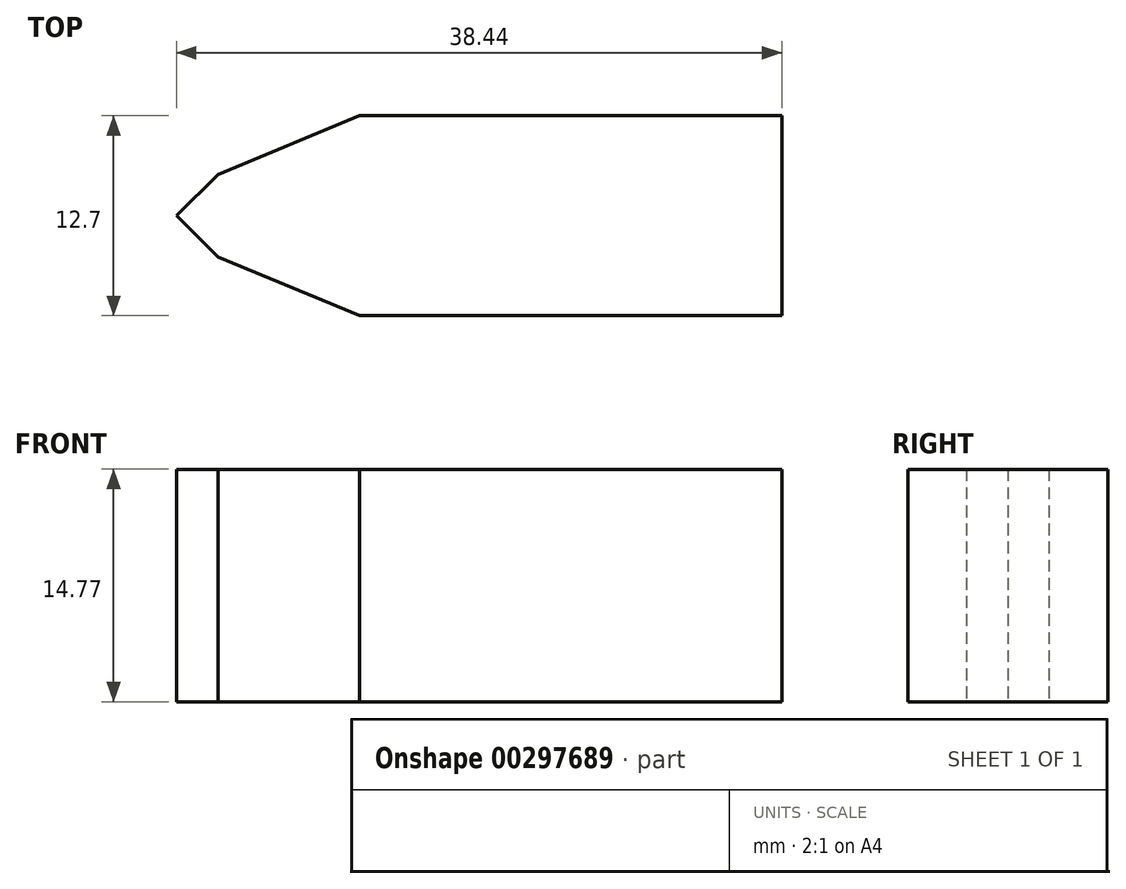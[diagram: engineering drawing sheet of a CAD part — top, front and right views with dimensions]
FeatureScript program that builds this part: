
annotation { "Feature Type Name" : "Feature", "Feature Type Description" : "" }
export const myFeature = defineFeature(function(context is Context, id is Id, definition is map)
    precondition{}
    {
        {
            var Q0;
            Q0=qCreatedBy(makeId("Front.planeOp"),FACE);
            var sketch = newSketch(context, id + "F0", { "sketchPlane" : qUnion([Q0])});
            skLineSegment(sketch, "E0", {"start": v(-0.02, -60.5) * mm, "end": v(-4.7, -60.5) * mm});
            skLineSegment(sketch, "E1", {"start": v(-0.02, 15.7) * mm, "end": v(-4.7, 15.7) * mm});
            skLineSegment(sketch, "E2", {"start": v(-4.7, 15.7) * mm, "end": v(-39.77, 15.7) * mm});
            skLineSegment(sketch, "E3", {"start": v(-39.77, 15.7) * mm, "end": v(-39.77, 30.46) * mm});
            skLineSegment(sketch, "E4", {"start": v(-0.02, 15.7) * mm, "end": v(5.02, 15.7) * mm});
            skLineSegment(sketch, "E5", {"start": v(5.02, 15.7) * mm, "end": v(5.02, 30.46) * mm});
            skLineSegment(sketch, "E6", {"start": v(5.02, 30.46) * mm, "end": v(-39.77, 30.46) * mm});
            skSolve(sketch);
        }
        {
            var Q0;
            Q0 = qSketchRegion(id + "F0", true);
            extrude(context, id + "F1", {"entities" : qUnion([Q0]), "depth" : 12.7 * mm});
        }
        {
            var Q0;
            Q0=makeQuery(id+"F1.opExtrude","CAP_EDGE",EDGE,{"disambiguationData":[OSD([sQuery(id+"F0.wireOp",EDGE,"E3")])],"isStart":false});
            var Q1;
            Q1=makeQuery(id+"F1.opExtrude","CAP_EDGE",EDGE,{"disambiguationData":[OSD([sQuery(id+"F0.wireOp",EDGE,"E3")])],"isStart":true});
            chamfer(context, id + "F2", {"entities" : qUnion([Q0, Q1]), "width" : 12.7 * mm, "tangentPropagation" : true});
        }
        {
            var Q0;
            {var subQ0=sQuery(id+"F0.wireOp",EDGE,"E3");Q0=makeQuery(id+"F2.opChamfer","BLEND_EDGE",EDGE,{"blendedFrom":[makeQuery(id+"F1.opExtrude","CAP_EDGE",EDGE,{"disambiguationData":[OSD([subQ0])],"isStart":false}),makeQuery(id+"F1.opExtrude","CAP_FACE",FACE,{"disambiguationData":[OSD([sQuery(id+"F0.wireOp",EDGE,"OZQ87AOx-t5jq-sSEw-11nk-o7TwbxqVxMWy"),sQuery(id+"F0.wireOp",EDGE,"yak0vyI2-Mmbg-dNsj-Fmrx-5NiHFIeQB878"),sQuery(id+"F0.wireOp",EDGE,"E0"),sQuery(id+"F0.wireOp",EDGE,"E2"),subQ0,sQuery(id+"F0.wireOp",EDGE,"E4"),sQuery(id+"F0.wireOp",EDGE,"E5"),sQuery(id+"F0.wireOp",EDGE,"E6")])],"isStart":false})],"blendedInto":[makeQuery(id+"F1.opExtrude","CAP_FACE",FACE,{"disambiguationData":[OSD([sQuery(id+"F0.wireOp",EDGE,"OZQ87AOx-t5jq-sSEw-11nk-o7TwbxqVxMWy"),sQuery(id+"F0.wireOp",EDGE,"yak0vyI2-Mmbg-dNsj-Fmrx-5NiHFIeQB878"),sQuery(id+"F0.wireOp",EDGE,"E0"),sQuery(id+"F0.wireOp",EDGE,"E2"),subQ0,sQuery(id+"F0.wireOp",EDGE,"E4"),sQuery(id+"F0.wireOp",EDGE,"E5"),sQuery(id+"F0.wireOp",EDGE,"E6")])],"isStart":false})]});}
            var Q1;
            {var subQ0=sQuery(id+"F0.wireOp",EDGE,"E3");Q1=makeQuery(id+"F2.opChamfer","BLEND_EDGE",EDGE,{"blendedFrom":[makeQuery(id+"F1.opExtrude","CAP_EDGE",EDGE,{"disambiguationData":[OSD([subQ0])],"isStart":true}),makeQuery(id+"F1.opExtrude","CAP_FACE",FACE,{"disambiguationData":[OSD([sQuery(id+"F0.wireOp",EDGE,"OZQ87AOx-t5jq-sSEw-11nk-o7TwbxqVxMWy"),sQuery(id+"F0.wireOp",EDGE,"yak0vyI2-Mmbg-dNsj-Fmrx-5NiHFIeQB878"),sQuery(id+"F0.wireOp",EDGE,"E0"),sQuery(id+"F0.wireOp",EDGE,"E2"),subQ0,sQuery(id+"F0.wireOp",EDGE,"E4"),sQuery(id+"F0.wireOp",EDGE,"E5"),sQuery(id+"F0.wireOp",EDGE,"E6")])],"isStart":true})],"blendedInto":[makeQuery(id+"F1.opExtrude","CAP_FACE",FACE,{"disambiguationData":[OSD([sQuery(id+"F0.wireOp",EDGE,"OZQ87AOx-t5jq-sSEw-11nk-o7TwbxqVxMWy"),sQuery(id+"F0.wireOp",EDGE,"yak0vyI2-Mmbg-dNsj-Fmrx-5NiHFIeQB878"),sQuery(id+"F0.wireOp",EDGE,"E0"),sQuery(id+"F0.wireOp",EDGE,"E2"),subQ0,sQuery(id+"F0.wireOp",EDGE,"E4"),sQuery(id+"F0.wireOp",EDGE,"E5"),sQuery(id+"F0.wireOp",EDGE,"E6")])],"isStart":true})]});}
            chamfer(context, id + "F3", {"entities" : qUnion([Q0, Q1]), "width" : 12.7 * mm, "tangentPropagation" : true});
        }
    });
